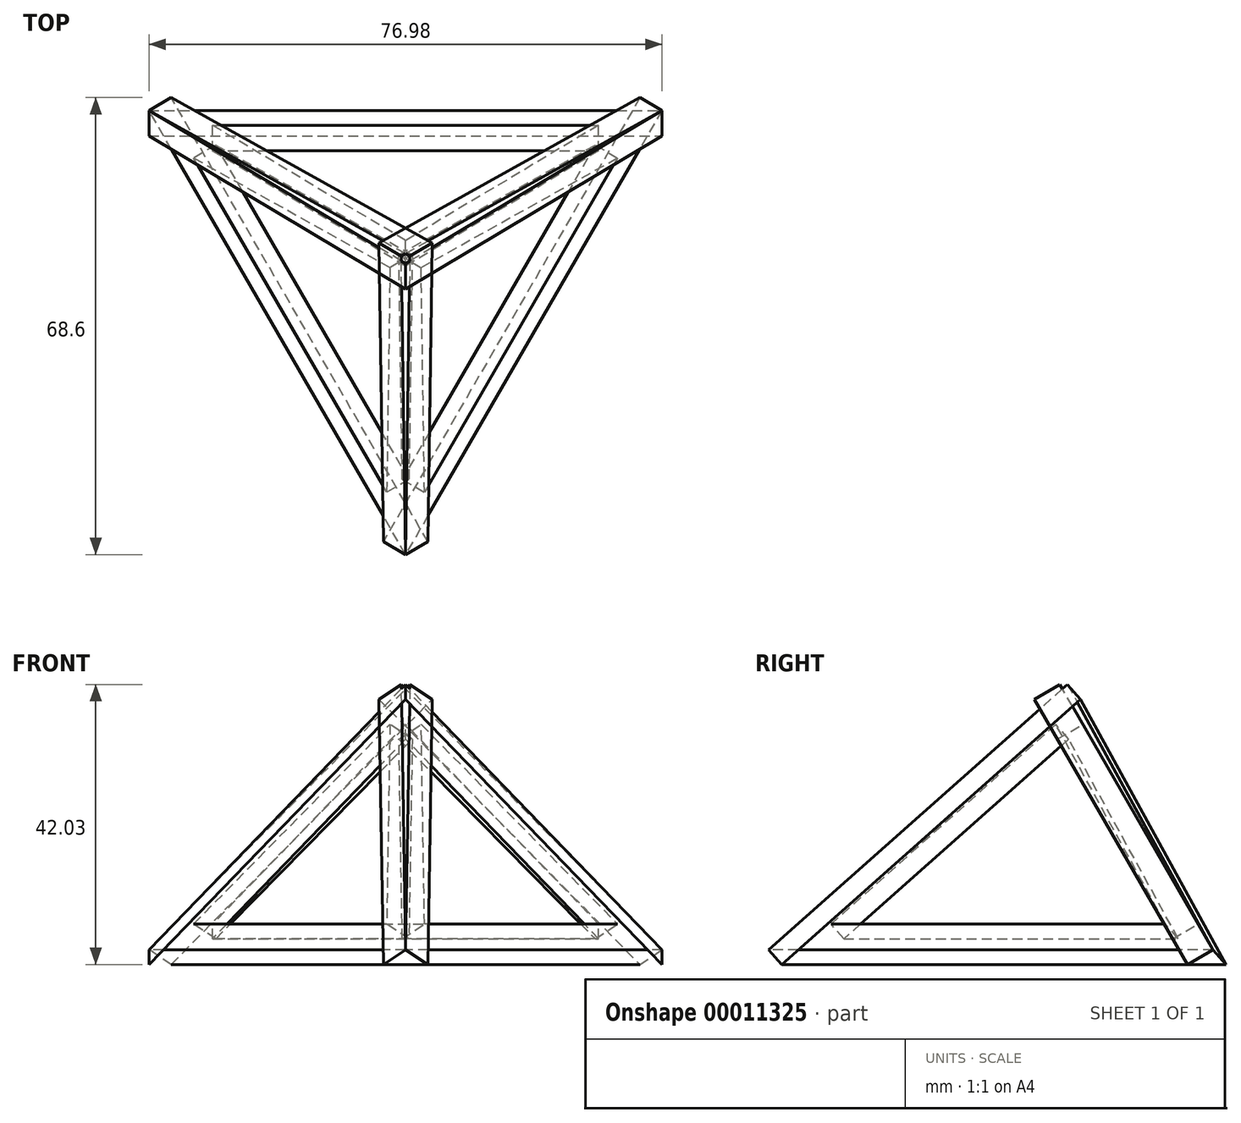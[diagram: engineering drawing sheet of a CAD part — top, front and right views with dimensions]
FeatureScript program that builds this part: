
annotation { "Feature Type Name" : "Feature", "Feature Type Description" : "" }
export const myFeature = defineFeature(function(context is Context, id is Id, definition is map)
    precondition{}
    {
        {
            var Q0;
            Q0=qCreatedBy(makeId("Top.planeOp"),FACE);
            var sketch = newSketch(context, id + "F0", { "sketchPlane" : qUnion([Q0])});
            skCircle(sketch, "E0", {"center": v(0, 0) * mm, "radius": 38.1 * mm, "construction": true});
            skCircle(sketch, "E1.cCircle", {"center": v(0, 0) * mm, "radius": 22.23 * mm, "construction": true});
            skLineSegment(sketch, "E1.0", {"start": v(0, -44.45) * mm, "end": v(-38.5, 22.23) * mm, "construction": true});
            skLineSegment(sketch, "E1.1", {"start": v(-38.5, 22.22) * mm, "end": v(38.5, 22.22) * mm, "construction": true});
            skLineSegment(sketch, "E1.2", {"start": v(38.5, 22.22) * mm, "end": v(0, -44.45) * mm, "construction": true});
            skPoint(sketch, "E1.0.midPoint", {"position": v(-19.25, -11.11) * mm});
            skSolve(sketch);
        }
        {
            var Q0;
            Q0=sQuery(id+"F0.wireOp",EDGE,"E1.0");
            cPlane(context, id + "F1", {"entities" : qUnion([Q0]), "cplaneType" : CPlaneType.LINE_ANGLE, "offset" : 152.4 * mm, "angle" : 120 * degree, "width" : 152.4 * mm, "height" : 152.4 * mm});
        }
        {
            var Q0;
            Q0=qCreatedBy(id+"F1.planeOp",FACE);
            var sketch = newSketch(context, id + "F2", { "sketchPlane" : qUnion([Q0])});
            skLineSegment(sketch, "E2.0", {"start": v(-40.07, 0) * mm, "end": v(33.9, -21.35) * mm});
            skLineSegment(sketch, "E3", {"start": v(33.9, -21.35) * mm, "end": v(9.67, 33.49) * mm});
            skLineSegment(sketch, "E4", {"start": v(9.67, 33.49) * mm, "end": v(-40.07, 0) * mm});
            skLineSegment(sketch, "E5.0", {"start": v(7.75, 26.84) * mm, "end": v(-29.69, 1.63) * mm});
            skLineSegment(sketch, "E5.1", {"start": v(25.99, -14.44) * mm, "end": v(7.75, 26.84) * mm});
            skLineSegment(sketch, "E5.2", {"start": v(-29.69, 1.63) * mm, "end": v(25.99, -14.44) * mm});
            skSolve(sketch);
        }
        {
            var Q0;
            Q0=makeQuery(id+"F2.imprint","IMPRINT",FACE,{"disambiguationData":[TD([[makeQuery(id+"F2.imprint","IMPRINT",EDGE,{"derivedFrom":sQuery(id+"F2.wireOp",EDGE,"E2.0")}),1.0]])]});
            extrude(context, id + "F3", {"entities" : qUnion([Q0]), "depth" : 4.44 * mm});
        }
        {
            var Q0;
            Q0=qCreatedBy(makeId("Front.planeOp"),FACE);
            var sketch = newSketch(context, id + "F4", { "sketchPlane" : qUnion([Q0])});
            skLineSegment(sketch, "E6", {"start": v(0, 0) * mm, "end": v(0, 25.68) * mm, "construction": true});
            skSolve(sketch);
        }
        {
            var Q0;
            Q0=makeQuery(id+"F3.opExtrude","SWEPT_BODY",BODY,{"disambiguationData":[OSD([sQuery(id+"F2.wireOp",EDGE,"E2.0"),sQuery(id+"F2.wireOp",EDGE,"29171d37-cd8e-45e4-961e-409b91bc00e3"),sQuery(id+"F2.wireOp",EDGE,"e8d04862-69ad-4c49-98c8-29a786dcc20d"),sQuery(id+"F2.wireOp",EDGE,"5eaee47a-c5f6-4067-97bc-7fbdf9b243a1.0"),sQuery(id+"F2.wireOp",EDGE,"5eaee47a-c5f6-4067-97bc-7fbdf9b243a1.1"),sQuery(id+"F2.wireOp",EDGE,"5eaee47a-c5f6-4067-97bc-7fbdf9b243a1.2")])]});
            var Q1;
            Q1=sQuery(id+"F4.wireOp",EDGE,"E6");
            circularPattern(context, id + "F5", {"entities" : qUnion([Q0]), "axis" : qUnion([Q1]), "angle" : 120 * degree, "instanceCount" : round(3)});
        }
    });
